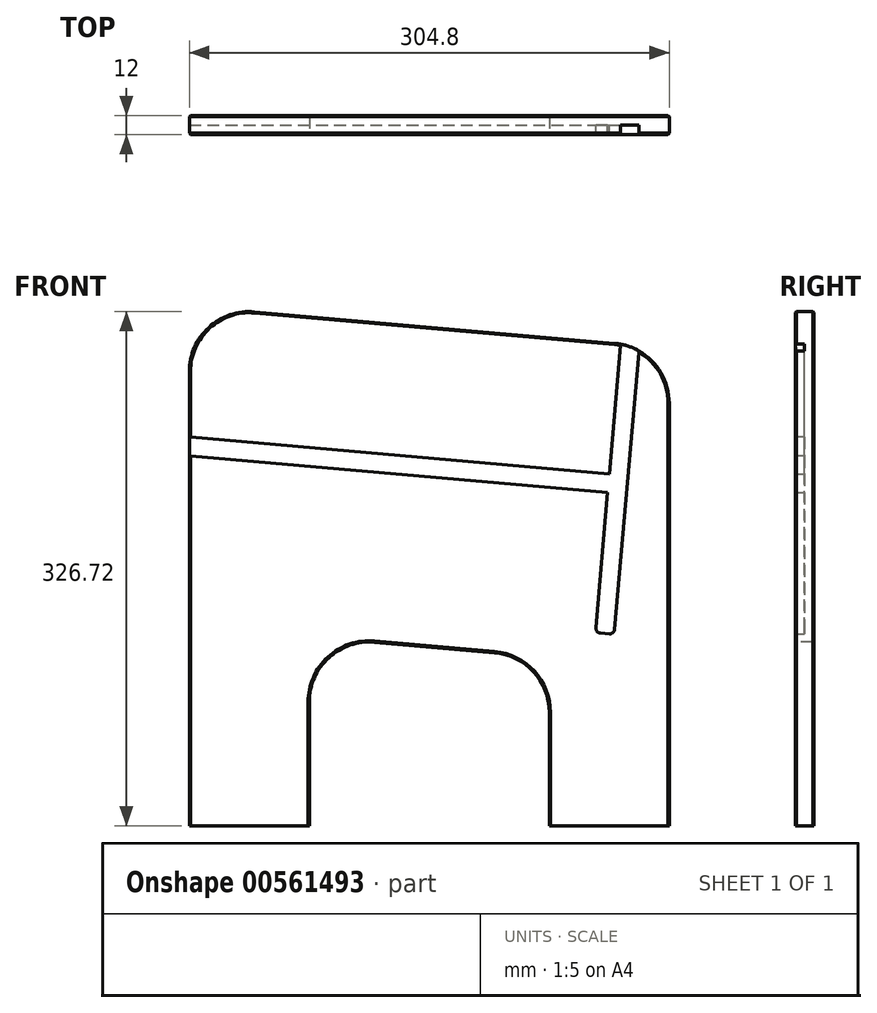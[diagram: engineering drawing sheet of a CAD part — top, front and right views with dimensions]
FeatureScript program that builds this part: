
annotation { "Feature Type Name" : "Feature", "Feature Type Description" : "" }
export const myFeature = defineFeature(function(context is Context, id is Id, definition is map)
    precondition{}
    {
        {
            var Q0;
            Q0=qCreatedBy(makeId("Front.planeOp"),FACE);
            var sketch = newSketch(context, id + "F0", { "sketchPlane" : qUnion([Q0])});
            skLineSegment(sketch, "E0", {"start": v(-76.2, 0) * mm, "end": v(-152.4, 0) * mm});
            skLineSegment(sketch, "E1", {"start": v(-152.4, 0) * mm, "end": v(-152.4, 288.62) * mm});
            skLineSegment(sketch, "E2", {"start": v(-110.98, 326.58) * mm, "end": v(117.62, 306.58) * mm});
            skLineSegment(sketch, "E3", {"start": v(152.4, 268.62) * mm, "end": v(152.4, 0) * mm});
            skLineSegment(sketch, "E4", {"start": v(152.4, 0) * mm, "end": v(76.2, 0) * mm});
            skLineSegment(sketch, "E5", {"start": v(76.2, 0) * mm, "end": v(76.2, 72.09) * mm});
            skLineSegment(sketch, "E6", {"start": v(41.42, 110.04) * mm, "end": v(-34.78, 116.7) * mm});
            skLineSegment(sketch, "E7", {"start": v(-76.2, 78.75) * mm, "end": v(-76.2, 0) * mm});
            skLineSegment(sketch, "E8", {"start": v(-76.2, 0) * mm, "end": v(76.2, 0) * mm, "construction": true});
            skPoint(sketch, "E9.visualSharp", {"position": v(-152.4, 330.2) * mm});
            skArc(sketch, "E9.filletArc", {"start": v(-110.98, 326.58) * mm, "mid": v(-140.04, 316.71) * mm, "end": v(-152.4, 288.62) * mm});
            skPoint(sketch, "E10.visualSharp", {"position": v(152.4, 303.53) * mm});
            skArc(sketch, "E10.filletArc", {"start": v(152.4, 268.62) * mm, "mid": v(142.4, 294.36) * mm, "end": v(117.62, 306.58) * mm});
            skPoint(sketch, "E11.visualSharp", {"position": v(-76.2, 120.33) * mm});
            skArc(sketch, "E11.filletArc", {"start": v(-34.78, 116.7) * mm, "mid": v(-63.84, 106.84) * mm, "end": v(-76.2, 78.75) * mm});
            skPoint(sketch, "E12.visualSharp", {"position": v(76.2, 107) * mm});
            skArc(sketch, "E12.filletArc", {"start": v(76.2, 72.09) * mm, "mid": v(66.2, 97.83) * mm, "end": v(41.42, 110.04) * mm});
            skLineSegment(sketch, "E13", {"start": v(-34.78, 116.7) * mm, "end": v(-152.4, 127) * mm, "construction": true});
            skLineSegment(sketch, "E14", {"start": v(-76.2, 0) * mm, "end": v(-76.2, 197.84) * mm, "construction": true});
            skLineSegment(sketch, "E15", {"start": v(-110.98, 326.58) * mm, "end": v(-262.29, 339.81) * mm, "construction": true});
            skLineSegment(sketch, "E16", {"start": v(-152.4, 0) * mm, "end": v(-152.4, 497.67) * mm, "construction": true});
            skSolve(sketch);
        }
        {
            var Q0;
            Q0=qSketchRegion(id+"F0",true);
            extrude(context, id + "F1", {"entities" : qUnion([Q0]), "oppositeDirection" : true, "depth" : 12 * mm, "offsetDistance" : 25.4 * mm, "symmetric" : true});
        }
        {
            var Q0;
            Q0=qCreatedBy(makeId("Front.planeOp"),FACE);
            var sketch = newSketch(context, id + "F2", { "sketchPlane" : qUnion([Q0])});
            skLineSegment(sketch, "E17", {"start": v(-152.4, 247) * mm, "end": v(114.33, 223.66) * mm});
            skLineSegment(sketch, "E18", {"start": v(114.33, 223.66) * mm, "end": v(121.87, 309.82) * mm});
            skLineSegment(sketch, "E19", {"start": v(121.87, 309.82) * mm, "end": v(133.82, 308.78) * mm});
            skLineSegment(sketch, "E20", {"start": v(133.82, 308.78) * mm, "end": v(117.98, 127.73) * mm});
            skLineSegment(sketch, "E21", {"start": v(-152.4, 234.95) * mm, "end": v(113.29, 211.7) * mm});
            skLineSegment(sketch, "E22", {"start": v(113.29, 211.7) * mm, "end": v(106.03, 128.77) * mm});
            skArc(sketch, "E23", {"start": v(106.03, 128.77) * mm, "mid": v(111.48, 122.27) * mm, "end": v(117.98, 127.73) * mm, "construction": true});
            skLineSegment(sketch, "E24", {"start": v(-152.4, 240.97) * mm, "end": v(200.35, 210.11) * mm, "construction": true});
            skLineSegment(sketch, "E25", {"start": v(106.03, 128.77) * mm, "end": v(105.78, 125.96) * mm});
            skLineSegment(sketch, "E26", {"start": v(108.67, 122.52) * mm, "end": v(114.3, 122.03) * mm});
            skLineSegment(sketch, "E27", {"start": v(117.74, 124.91) * mm, "end": v(117.98, 127.73) * mm});
            skPoint(sketch, "E28.0.visualSharp", {"position": v(105.5, 122.8) * mm});
            skArc(sketch, "E28.0.filletArc", {"start": v(105.78, 125.96) * mm, "mid": v(106.51, 123.64) * mm, "end": v(108.67, 122.52) * mm});
            skPoint(sketch, "E28.1.visualSharp", {"position": v(117.46, 121.75) * mm});
            skArc(sketch, "E28.1.filletArc", {"start": v(114.3, 122.03) * mm, "mid": v(116.62, 122.76) * mm, "end": v(117.74, 124.91) * mm});
            skLineSegment(sketch, "E29", {"start": v(-152.4, 247) * mm, "end": v(-156.2, 247.33) * mm});
            skLineSegment(sketch, "E30", {"start": v(-156.2, 247.33) * mm, "end": v(-157.24, 235.37) * mm});
            skLineSegment(sketch, "E31", {"start": v(-157.24, 235.37) * mm, "end": v(-152.4, 234.95) * mm});
            skPoint(sketch, "E32", {"position": v(121.54, 306.03) * mm});
            skSolve(sketch);
        }
        {
            var Q0;
            Q0=qSketchRegion(id+"F2",true);
            extrude(context, id + "F3", {"entities" : qUnion([Q0]), "operationType" : NewBodyOperationType.REMOVE, "depth" : 6.35 * mm, "offsetDistance" : 25.4 * mm});
        }
        {
            var Q0;
            Q0=makeQuery(id+"F1.opExtrude","CAP_EDGE",EDGE,{"disambiguationData":[OSD([sQuery(id+"F0.wireOp",EDGE,"E2")])],"isStart":false});
            var Q1;
            Q1=makeQuery(id+"F1.opExtrude","CAP_EDGE",EDGE,{"disambiguationData":[OSD([sQuery(id+"F0.wireOp",EDGE,"E6")])],"isStart":false});
            var Q2;
            Q2=makeQuery(id+"F1.opExtrude","CAP_EDGE",EDGE,{"disambiguationData":[OSD([sQuery(id+"F0.wireOp",EDGE,"E2")])],"isStart":true});
            var Q3;
            Q3=makeQuery(id+"F1.opExtrude","CAP_EDGE",EDGE,{"disambiguationData":[OSD([sQuery(id+"F0.wireOp",EDGE,"E3")])],"isStart":true});
            var Q4;
            {var subQ0=sQuery(id+"F0.wireOp",EDGE,"E0");var subQ1=sQuery(id+"F0.wireOp",EDGE,"E1");Q4=makeQuery(id+"F3.boolean.opBoolean","SPLIT",EDGE,{"disambiguationData":[TD([makeQuery(id+"F1.opExtrude","SWEPT_FACE",FACE,{"disambiguationData":[OSD([subQ0])]})])],"derivedFrom":makeQuery(id+"F1.opExtrude","CAP_EDGE",EDGE,{"disambiguationData":[OSD([subQ1])],"isStart":true})});}
            var Q5;
            Q5=makeQuery(id+"F1.opExtrude","CAP_EDGE",EDGE,{"disambiguationData":[OSD([sQuery(id+"F0.wireOp",EDGE,"E6")])],"isStart":true});
            chamfer(context, id + "F4", {"entities" : qUnion([Q0, Q1, Q2, Q3, Q4, Q5]), "width" : 0.76 * mm, "tangentPropagation" : true});
        }
    });
